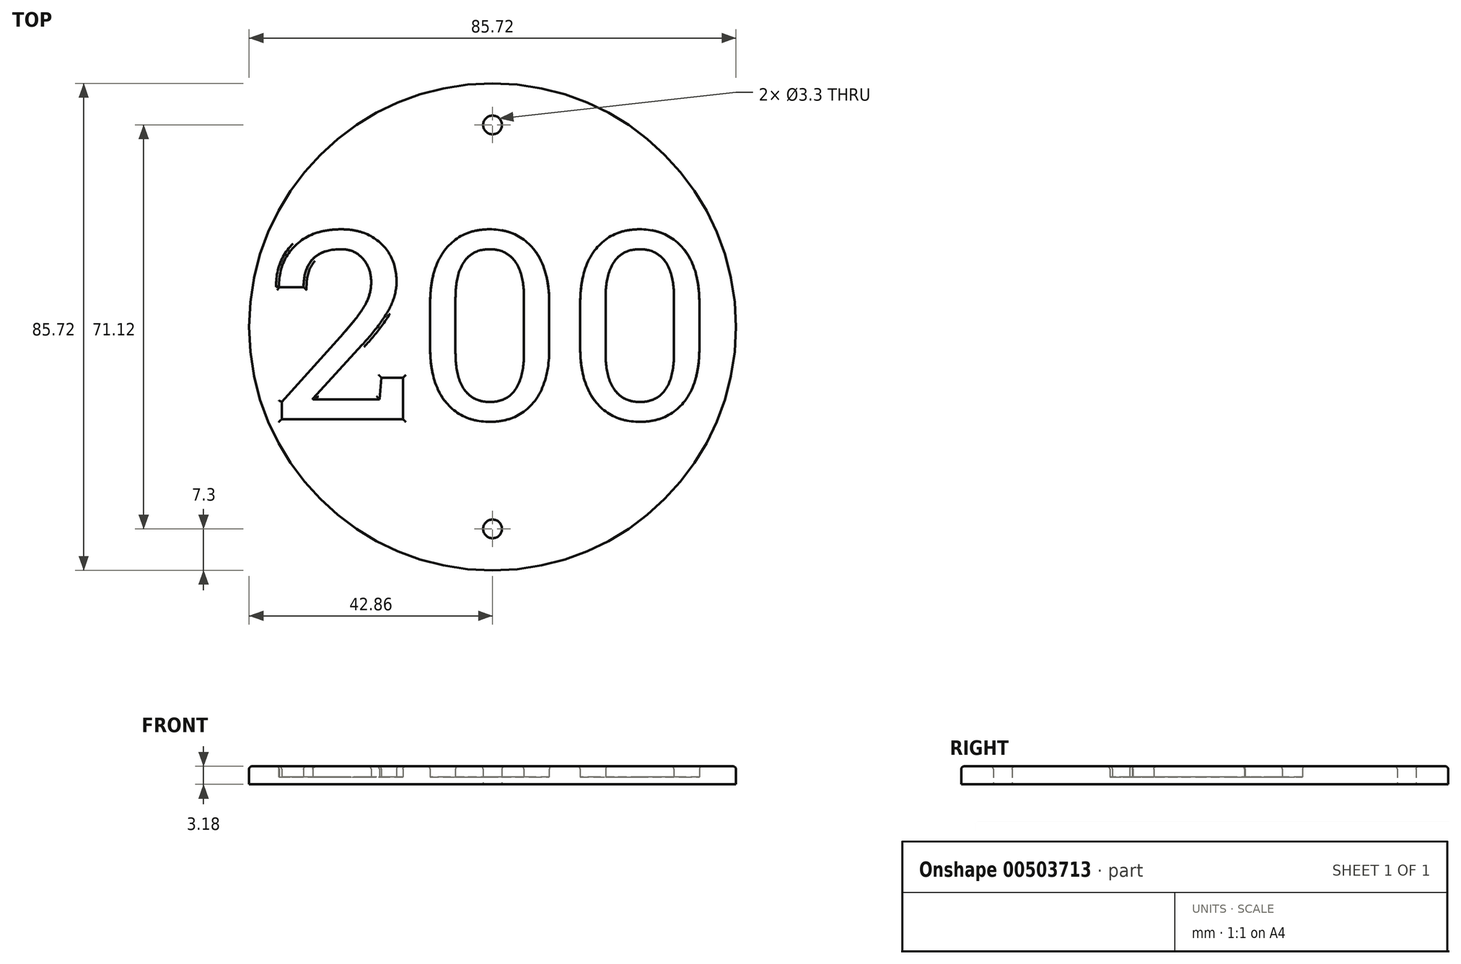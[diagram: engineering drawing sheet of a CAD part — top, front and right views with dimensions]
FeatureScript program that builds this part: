
annotation { "Feature Type Name" : "Feature", "Feature Type Description" : "" }
export const myFeature = defineFeature(function(context is Context, id is Id, definition is map)
    precondition{}
    {
        {
            var Q0;
            Q0=qCreatedBy(makeId("Top.planeOp"),FACE);
            var sketch = newSketch(context, id + "F0", { "sketchPlane" : qUnion([Q0])});
            skCircle(sketch, "E0", {"center": v(0, 0) * mm, "radius": 42.86 * mm});
            skText(sketch, "E1", { "text": "200", "fontName": "RobotoSlab-Regular.ttf"});
            skCircle(sketch, "E2", {"center": v(0, 35.56) * mm, "radius": 1.65 * mm});
            skCircle(sketch, "E3", {"center": v(0, -35.56) * mm, "radius": 1.65 * mm});
            const initialGuessF0  = {"E1": [-0.0393, -0.01623, 1, 0, 0.03336]};
            skSetInitialGuess(sketch, initialGuessF0);
            skSolve(sketch);
        }
        {
            var Q0;
            Q0 = qSketchRegion(id + "F0", true);
            var Q1;
            Q1=makeQuery(id+"F0.imprint","IMPRINT",FACE,{"disambiguationData":[TD([[makeQuery(id+"F0.imprint","IMPRINT",EDGE,{"derivedFrom":sQuery(id+"F0.wireOp",EDGE,"E1.sketch_text.stroke-33")}),1.0]])]});
            var Q2;
            Q2=makeQuery(id+"F0.imprint","IMPRINT",FACE,{"disambiguationData":[TD([[makeQuery(id+"F0.imprint","IMPRINT",EDGE,{"derivedFrom":sQuery(id+"F0.wireOp",EDGE,"E1.sketch_text.stroke-53")}),1.0]])]});
            extrude(context, id + "F1", {"entities" : qUnion([Q0, Q1, Q2]), "depth" : 1.9 * mm});
        }
        {
            var Q0;
            Q0=makeQuery(id+"F1.opExtrude","CAP_FACE",FACE,{"disambiguationData":[OSD([sQuery(id+"F0.wireOp",EDGE,"E0"),sQuery(id+"F0.wireOp",EDGE,"E1.sketch_text.stroke-0"),sQuery(id+"F0.wireOp",EDGE,"E1.sketch_text.stroke-1"),sQuery(id+"F0.wireOp",EDGE,"E1.sketch_text.stroke-2"),sQuery(id+"F0.wireOp",EDGE,"E1.sketch_text.stroke-3"),sQuery(id+"F0.wireOp",EDGE,"E1.sketch_text.stroke-4"),sQuery(id+"F0.wireOp",EDGE,"E1.sketch_text.stroke-5"),sQuery(id+"F0.wireOp",EDGE,"E1.sketch_text.stroke-6"),sQuery(id+"F0.wireOp",EDGE,"E1.sketch_text.stroke-7"),sQuery(id+"F0.wireOp",EDGE,"E1.sketch_text.stroke-8"),sQuery(id+"F0.wireOp",EDGE,"E1.sketch_text.stroke-9"),sQuery(id+"F0.wireOp",EDGE,"E1.sketch_text.stroke-10"),sQuery(id+"F0.wireOp",EDGE,"E1.sketch_text.stroke-11"),sQuery(id+"F0.wireOp",EDGE,"E1.sketch_text.stroke-12"),sQuery(id+"F0.wireOp",EDGE,"E1.sketch_text.stroke-13"),sQuery(id+"F0.wireOp",EDGE,"E1.sketch_text.stroke-14"),sQuery(id+"F0.wireOp",EDGE,"E1.sketch_text.stroke-15"),sQuery(id+"F0.wireOp",EDGE,"E1.sketch_text.stroke-16"),sQuery(id+"F0.wireOp",EDGE,"E1.sketch_text.stroke-17"),sQuery(id+"F0.wireOp",EDGE,"E1.sketch_text.stroke-18"),sQuery(id+"F0.wireOp",EDGE,"E1.sketch_text.stroke-19"),sQuery(id+"F0.wireOp",EDGE,"E1.sketch_text.stroke-20"),sQuery(id+"F0.wireOp",EDGE,"E1.sketch_text.stroke-21"),sQuery(id+"F0.wireOp",EDGE,"E1.sketch_text.stroke-22"),sQuery(id+"F0.wireOp",EDGE,"E1.sketch_text.stroke-23"),sQuery(id+"F0.wireOp",EDGE,"E1.sketch_text.stroke-24"),sQuery(id+"F0.wireOp",EDGE,"E1.sketch_text.stroke-25"),sQuery(id+"F0.wireOp",EDGE,"E1.sketch_text.stroke-26"),sQuery(id+"F0.wireOp",EDGE,"E1.sketch_text.stroke-27"),sQuery(id+"F0.wireOp",EDGE,"E1.sketch_text.stroke-28"),sQuery(id+"F0.wireOp",EDGE,"E1.sketch_text.stroke-29"),sQuery(id+"F0.wireOp",EDGE,"E1.sketch_text.stroke-30"),sQuery(id+"F0.wireOp",EDGE,"E1.sketch_text.stroke-31"),sQuery(id+"F0.wireOp",EDGE,"E1.sketch_text.stroke-32"),sQuery(id+"F0.wireOp",EDGE,"E1.sketch_text.stroke-33"),sQuery(id+"F0.wireOp",EDGE,"E1.sketch_text.stroke-34"),sQuery(id+"F0.wireOp",EDGE,"E1.sketch_text.stroke-35"),sQuery(id+"F0.wireOp",EDGE,"E1.sketch_text.stroke-36"),sQuery(id+"F0.wireOp",EDGE,"E1.sketch_text.stroke-37"),sQuery(id+"F0.wireOp",EDGE,"E1.sketch_text.stroke-38"),sQuery(id+"F0.wireOp",EDGE,"E1.sketch_text.stroke-39"),sQuery(id+"F0.wireOp",EDGE,"E1.sketch_text.stroke-40"),sQuery(id+"F0.wireOp",EDGE,"E1.sketch_text.stroke-41"),sQuery(id+"F0.wireOp",EDGE,"E1.sketch_text.stroke-42"),sQuery(id+"F0.wireOp",EDGE,"E1.sketch_text.stroke-43"),sQuery(id+"F0.wireOp",EDGE,"E1.sketch_text.stroke-44"),sQuery(id+"F0.wireOp",EDGE,"E1.sketch_text.stroke-45"),sQuery(id+"F0.wireOp",EDGE,"E1.sketch_text.stroke-46"),sQuery(id+"F0.wireOp",EDGE,"E1.sketch_text.stroke-47"),sQuery(id+"F0.wireOp",EDGE,"E1.sketch_text.stroke-48"),sQuery(id+"F0.wireOp",EDGE,"E1.sketch_text.stroke-49"),sQuery(id+"F0.wireOp",EDGE,"E1.sketch_text.stroke-50"),sQuery(id+"F0.wireOp",EDGE,"E1.sketch_text.stroke-51"),sQuery(id+"F0.wireOp",EDGE,"E1.sketch_text.stroke-52"),sQuery(id+"F0.wireOp",EDGE,"E1.sketch_text.stroke-53"),sQuery(id+"F0.wireOp",EDGE,"E1.sketch_text.stroke-54"),sQuery(id+"F0.wireOp",EDGE,"E1.sketch_text.stroke-55"),sQuery(id+"F0.wireOp",EDGE,"E1.sketch_text.stroke-56"),sQuery(id+"F0.wireOp",EDGE,"E1.sketch_text.stroke-57"),sQuery(id+"F0.wireOp",EDGE,"E1.sketch_text.stroke-58"),sQuery(id+"F0.wireOp",EDGE,"E1.sketch_text.stroke-59"),sQuery(id+"F0.wireOp",EDGE,"E1.sketch_text.stroke-60"),sQuery(id+"F0.wireOp",EDGE,"E1.sketch_text.stroke-61"),sQuery(id+"F0.wireOp",EDGE,"E1.sketch_text.stroke-62"),sQuery(id+"F0.wireOp",EDGE,"E1.sketch_text.stroke-63"),sQuery(id+"F0.wireOp",EDGE,"E1.sketch_text.stroke-64"),sQuery(id+"F0.wireOp",EDGE,"E1.sketch_text.stroke-65"),sQuery(id+"F0.wireOp",EDGE,"E1.sketch_text.stroke-66"),sQuery(id+"F0.wireOp",EDGE,"E1.sketch_text.stroke-67"),sQuery(id+"F0.wireOp",EDGE,"E1.sketch_text.stroke-68"),sQuery(id+"F0.wireOp",EDGE,"E1.sketch_text.stroke-69"),sQuery(id+"F0.wireOp",EDGE,"E1.sketch_text.stroke-70"),sQuery(id+"F0.wireOp",EDGE,"E1.sketch_text.stroke-71"),sQuery(id+"F0.wireOp",EDGE,"E1.sketch_text.stroke-72"),sQuery(id+"F0.wireOp",EDGE,"E1.sketch_text.stroke-73"),sQuery(id+"F0.wireOp",EDGE,"E1.sketch_text.stroke-74"),sQuery(id+"F0.wireOp",EDGE,"E1.sketch_text.stroke-75"),sQuery(id+"F0.wireOp",EDGE,"E1.sketch_text.stroke-76"),sQuery(id+"F0.wireOp",EDGE,"E1.sketch_text.stroke-77"),sQuery(id+"F0.wireOp",EDGE,"E1.sketch_text.stroke-78"),sQuery(id+"F0.wireOp",EDGE,"E1.sketch_text.stroke-79"),sQuery(id+"F0.wireOp",EDGE,"E1.sketch_text.stroke-80"),sQuery(id+"F0.wireOp",EDGE,"E1.sketch_text.stroke-81"),sQuery(id+"F0.wireOp",EDGE,"E1.sketch_text.stroke-82"),sQuery(id+"F0.wireOp",EDGE,"E1.sketch_text.stroke-83"),sQuery(id+"F0.wireOp",EDGE,"E1.sketch_text.stroke-84"),sQuery(id+"F0.wireOp",EDGE,"E1.sketch_text.stroke-85"),sQuery(id+"F0.wireOp",EDGE,"E1.sketch_text.stroke-86"),sQuery(id+"F0.wireOp",EDGE,"E1.sketch_text.stroke-87"),sQuery(id+"F0.wireOp",EDGE,"E1.sketch_text.stroke-88"),sQuery(id+"F0.wireOp",EDGE,"E1.sketch_text.stroke-89"),sQuery(id+"F0.wireOp",EDGE,"E1.sketch_text.stroke-90"),sQuery(id+"F0.wireOp",EDGE,"E1.sketch_text.stroke-91"),sQuery(id+"F0.wireOp",EDGE,"E1.sketch_text.stroke-92"),sQuery(id+"F0.wireOp",EDGE,"E1.sketch_text.stroke-93"),sQuery(id+"F0.wireOp",EDGE,"E1.sketch_text.stroke-94"),sQuery(id+"F0.wireOp",EDGE,"E1.sketch_text.stroke-95"),sQuery(id+"F0.wireOp",EDGE,"E1.sketch_text.stroke-96"),sQuery(id+"F0.wireOp",EDGE,"E1.sketch_text.stroke-97"),sQuery(id+"F0.wireOp",EDGE,"E1.sketch_text.stroke-98")])],"isStart":false});
            var Q1;
            Q1=makeQuery(id+"F1.opExtrude","CAP_FACE",FACE,{"disambiguationData":[OSD([sQuery(id+"F0.wireOp",EDGE,"E1.sketch_text.stroke-33"),sQuery(id+"F0.wireOp",EDGE,"E1.sketch_text.stroke-34"),sQuery(id+"F0.wireOp",EDGE,"E1.sketch_text.stroke-35"),sQuery(id+"F0.wireOp",EDGE,"E1.sketch_text.stroke-36"),sQuery(id+"F0.wireOp",EDGE,"E1.sketch_text.stroke-37"),sQuery(id+"F0.wireOp",EDGE,"E1.sketch_text.stroke-38"),sQuery(id+"F0.wireOp",EDGE,"E1.sketch_text.stroke-39"),sQuery(id+"F0.wireOp",EDGE,"E1.sketch_text.stroke-40"),sQuery(id+"F0.wireOp",EDGE,"E1.sketch_text.stroke-41"),sQuery(id+"F0.wireOp",EDGE,"E1.sketch_text.stroke-42")])],"isStart":false});
            var Q2;
            Q2=makeQuery(id+"F1.opExtrude","CAP_FACE",FACE,{"disambiguationData":[OSD([sQuery(id+"F0.wireOp",EDGE,"E1.sketch_text.stroke-53"),sQuery(id+"F0.wireOp",EDGE,"E1.sketch_text.stroke-54"),sQuery(id+"F0.wireOp",EDGE,"E1.sketch_text.stroke-55"),sQuery(id+"F0.wireOp",EDGE,"E1.sketch_text.stroke-56"),sQuery(id+"F0.wireOp",EDGE,"E1.sketch_text.stroke-57"),sQuery(id+"F0.wireOp",EDGE,"E1.sketch_text.stroke-58"),sQuery(id+"F0.wireOp",EDGE,"E1.sketch_text.stroke-59"),sQuery(id+"F0.wireOp",EDGE,"E1.sketch_text.stroke-60"),sQuery(id+"F0.wireOp",EDGE,"E1.sketch_text.stroke-61"),sQuery(id+"F0.wireOp",EDGE,"E1.sketch_text.stroke-62")])],"isStart":false});
            fillet(context, id + "F2", {"entities" : qUnion([Q0, Q1, Q2]), "radius" : 0.5 * mm, "allowEdgeOverflow" : false});
        }
        {
            var Q0;
            Q0=qCreatedBy(makeId("Top.planeOp"),FACE);
            var sketch = newSketch(context, id + "F3", { "sketchPlane" : qUnion([Q0])});
            skCircle(sketch, "E4", {"center": v(0, 0) * mm, "radius": 42.86 * mm});
            skCircle(sketch, "E5", {"center": v(0, -35.56) * mm, "radius": 1.65 * mm});
            skCircle(sketch, "E6", {"center": v(0, 35.56) * mm, "radius": 1.65 * mm});
            skSolve(sketch);
        }
        {
            var Q0;
            Q0 = qSketchRegion(id + "F3", true);
            extrude(context, id + "F4", {"entities" : qUnion([Q0]), "operationType" : NewBodyOperationType.ADD, "oppositeDirection" : true, "depth" : 1.27 * mm});
        }
    });
